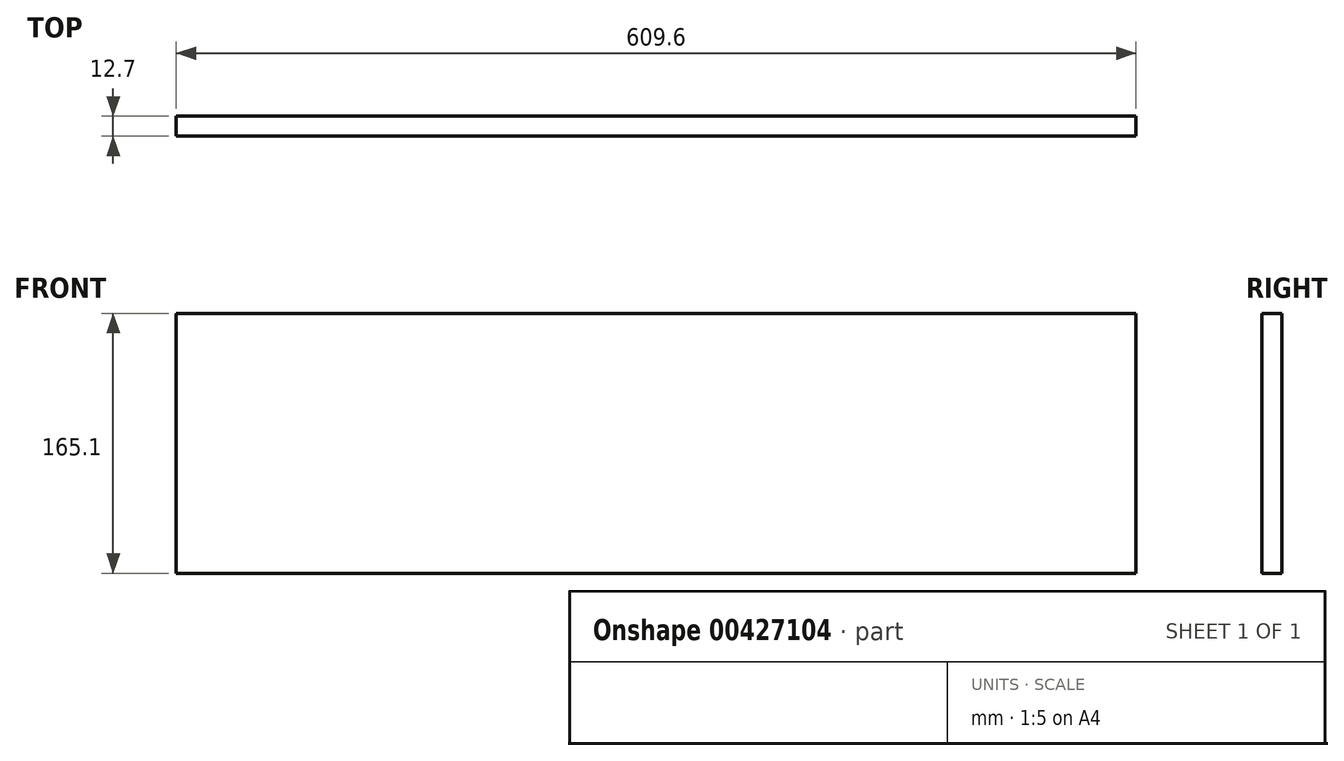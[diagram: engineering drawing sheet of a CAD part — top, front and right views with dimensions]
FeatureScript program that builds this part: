
annotation { "Feature Type Name" : "Feature", "Feature Type Description" : "" }
export const myFeature = defineFeature(function(context is Context, id is Id, definition is map)
    precondition{}
    {
        {
            var Q0;
            Q0=qCreatedBy(makeId("Front.planeOp"),FACE);
            var sketch = newSketch(context, id + "F0", { "sketchPlane" : qUnion([Q0])});
            skLineSegment(sketch, "E0.bottom", {"start": v(304.8, -82.55) * mm, "end": v(-304.8, -82.55) * mm});
            skLineSegment(sketch, "E0.top", {"start": v(304.8, 82.55) * mm, "end": v(-304.8, 82.55) * mm});
            skLineSegment(sketch, "E0.left", {"start": v(304.8, -82.55) * mm, "end": v(304.8, 82.55) * mm});
            skLineSegment(sketch, "E0.right", {"start": v(-304.8, -82.55) * mm, "end": v(-304.8, 82.55) * mm});
            skPoint(sketch, "E0.middle", {"position": v(0, 0) * mm});
            skSolve(sketch);
        }
        {
            var Q0;
            Q0=makeQuery(id+"F0.imprint","IMPRINT",FACE,{"disambiguationData":[TD([[makeQuery(id+"F0.imprint","IMPRINT",EDGE,{"derivedFrom":sQuery(id+"F0.wireOp",EDGE,"E0.bottom")}),-1.0]])]});
            extrude(context, id + "F1", {"entities" : qUnion([Q0]), "depth" : 12.7 * mm});
        }
    });
